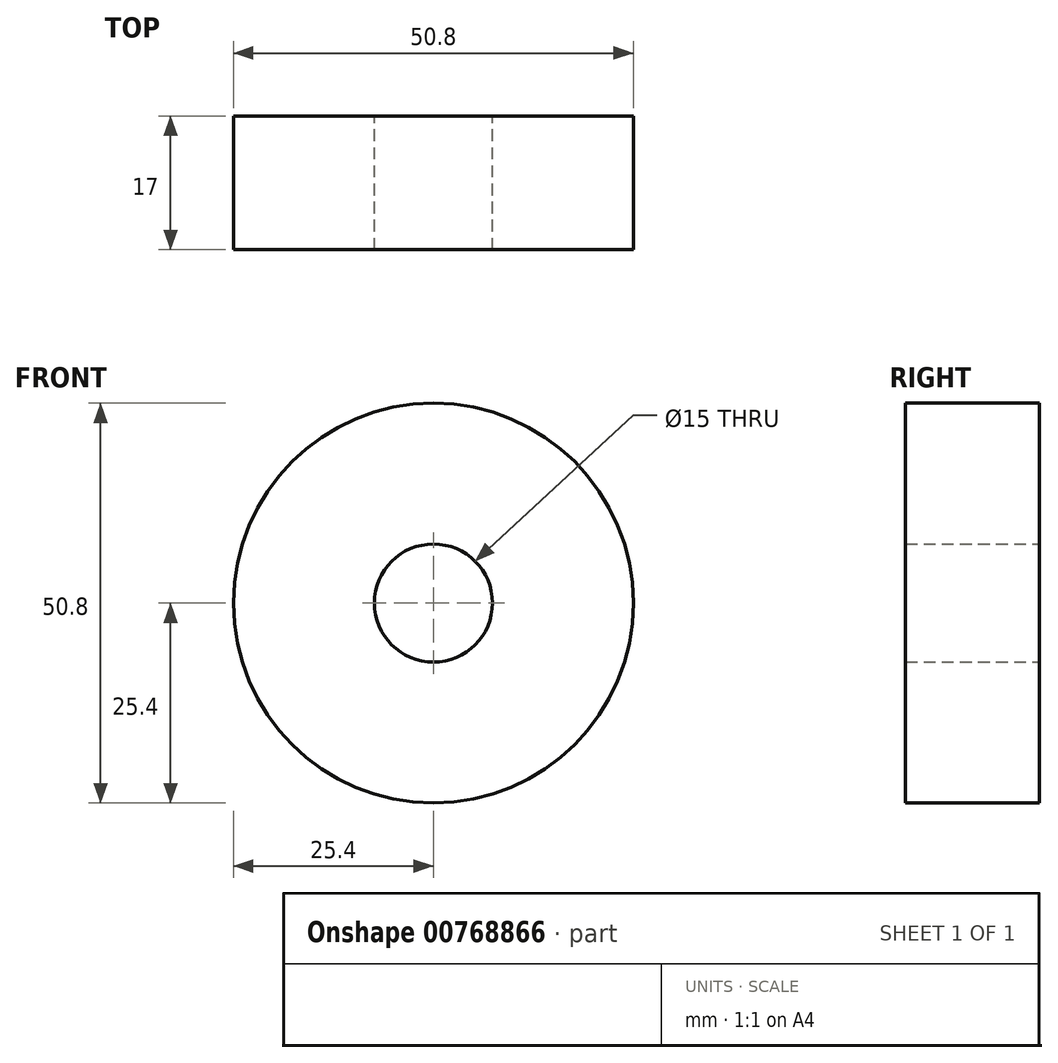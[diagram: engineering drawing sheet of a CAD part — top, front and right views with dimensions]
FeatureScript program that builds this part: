
annotation { "Feature Type Name" : "Feature", "Feature Type Description" : "" }
export const myFeature = defineFeature(function(context is Context, id is Id, definition is map)
    precondition{}
    {
        {
            var Q0;
            Q0=qCreatedBy(makeId("Front.planeOp"),FACE);
            var sketch = newSketch(context, id + "F0", { "sketchPlane" : qUnion([Q0])});
            skCircle(sketch, "E0", {"center": v(0, 0) * mm, "radius": 7.5 * mm});
            skCircle(sketch, "E1", {"center": v(0, 0) * mm, "radius": 25.4 * mm});
            skSolve(sketch);
        }
        {
            var Q0;
            Q0 = qSketchRegion(id + "F0", true);
            extrude(context, id + "F1", {"entities" : qUnion([Q0]), "depth" : 17 * mm, "offsetDistance" : 25 * mm});
        }
    });
